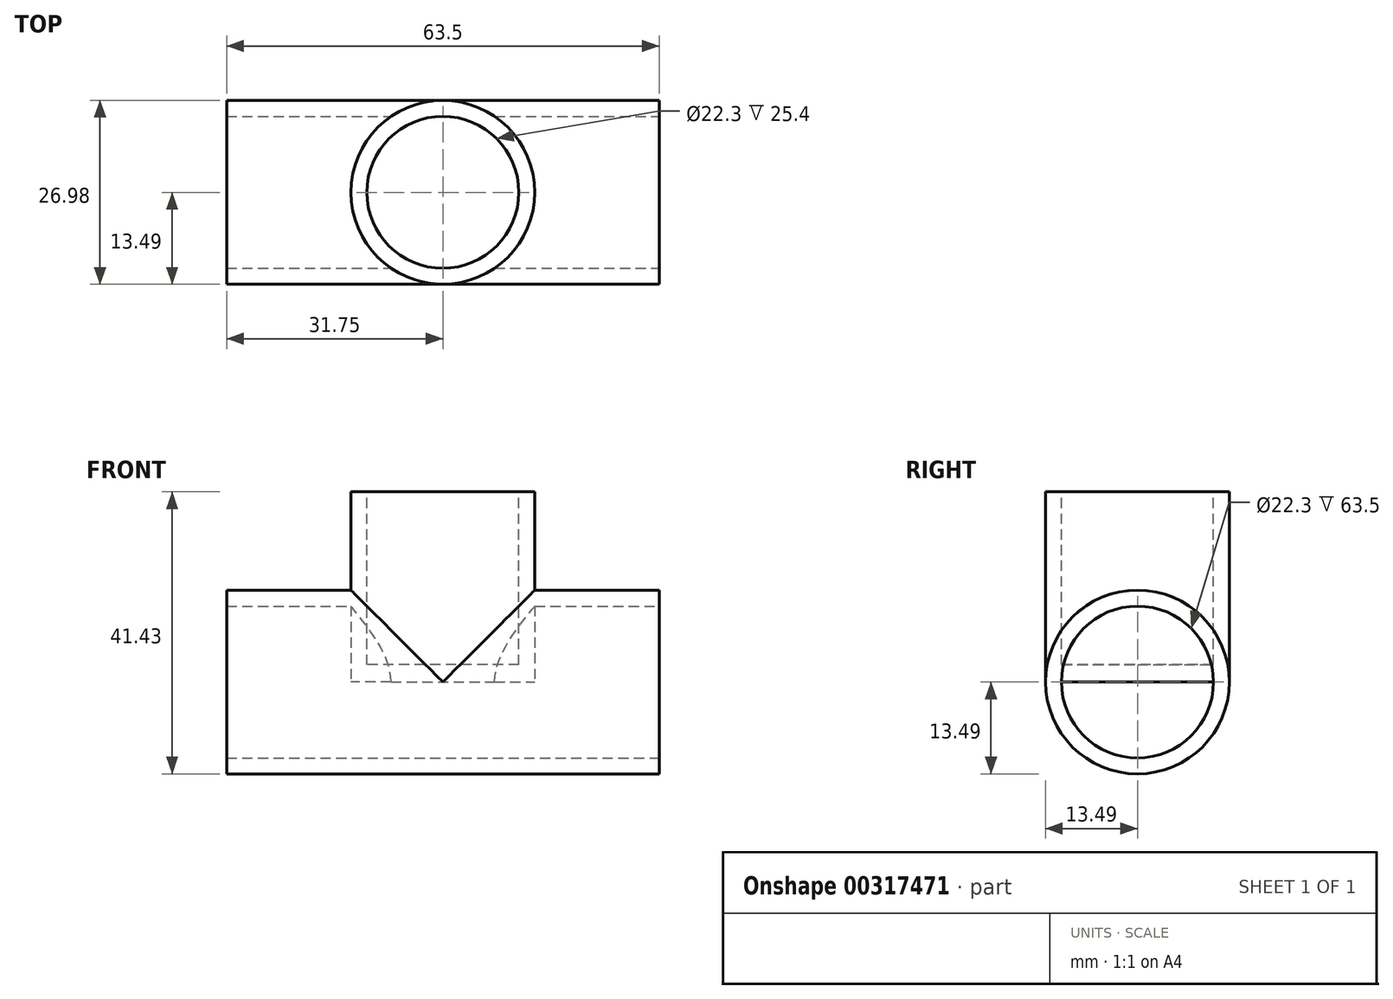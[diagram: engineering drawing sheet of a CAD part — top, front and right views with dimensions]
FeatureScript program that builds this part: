
annotation { "Feature Type Name" : "Feature", "Feature Type Description" : "" }
export const myFeature = defineFeature(function(context is Context, id is Id, definition is map)
    precondition{}
    {
        {
            var Q0;
            Q0=qCreatedBy(makeId("Right.planeOp"),FACE);
            var sketch = newSketch(context, id + "F0", { "sketchPlane" : qUnion([Q0])});
            skCircle(sketch, "E0", {"center": v(0, 0) * mm, "radius": 13.5 * mm});
            skSolve(sketch);
        }
        {
            var Q0;
            Q0=makeQuery(id+"F0.imprint","IMPRINT",FACE,{"disambiguationData":[TD([[makeQuery(id+"F0.imprint","IMPRINT",EDGE,{"derivedFrom":sQuery(id+"F0.wireOp",EDGE,"E0")}),1.0]])]});
            extrude(context, id + "F1", {"entities" : qUnion([Q0]), "endBound" : BoundingType.SYMMETRIC, "depth" : 63.5 * mm});
        }
        {
            var Q0;
            Q0=makeQuery(id+"F1.opExtrude","CAP_FACE",FACE,{"disambiguationData":[OSD([sQuery(id+"F0.wireOp",EDGE,"E0")])],"isStart":false});
            var sketch = newSketch(context, id + "F2", { "sketchPlane" : qUnion([Q0])});
            skCircle(sketch, "E1", {"center": v(0, 0) * mm, "radius": 11.15 * mm});
            skSolve(sketch);
        }
        {
            var Q0;
            Q0=makeQuery(id+"F2.imprint","IMPRINT",FACE,{"disambiguationData":[TD([[makeQuery(id+"F2.imprint","IMPRINT",EDGE,{"derivedFrom":sQuery(id+"F2.wireOp",EDGE,"E1")}),1.0]])]});
            extrude(context, id + "F3", {"entities" : qUnion([Q0]), "operationType" : NewBodyOperationType.REMOVE, "oppositeDirection" : true, "depth" : 63.5 * mm});
        }
        {
            var Q0;
            Q0=qCreatedBy(makeId("Top.planeOp"),FACE);
            var sketch = newSketch(context, id + "F4", { "sketchPlane" : qUnion([Q0])});
            skCircle(sketch, "E2", {"center": v(0, 0) * mm, "radius": 13.5 * mm});
            skSolve(sketch);
        }
        {
            var Q0;
            Q0 = qSketchRegion(id + "F4", true);
            extrude(context, id + "F5", {"entities" : qUnion([Q0]), "operationType" : NewBodyOperationType.ADD, "depth" : 27.94 * mm});
        }
        {
            var Q0;
            Q0=makeQuery(id+"F5.opExtrude","CAP_FACE",FACE,{"disambiguationData":[OSD([sQuery(id+"F4.wireOp",EDGE,"E2")])],"isStart":false});
            var sketch = newSketch(context, id + "F6", { "sketchPlane" : qUnion([Q0])});
            skCircle(sketch, "E3", {"center": v(0, 0) * mm, "radius": 11.15 * mm});
            skSolve(sketch);
        }
        {
            var Q0;
            Q0 = qSketchRegion(id + "F6", true);
            extrude(context, id + "F7", {"entities" : qUnion([Q0]), "operationType" : NewBodyOperationType.REMOVE, "oppositeDirection" : true, "depth" : 25.4 * mm});
        }
    });
